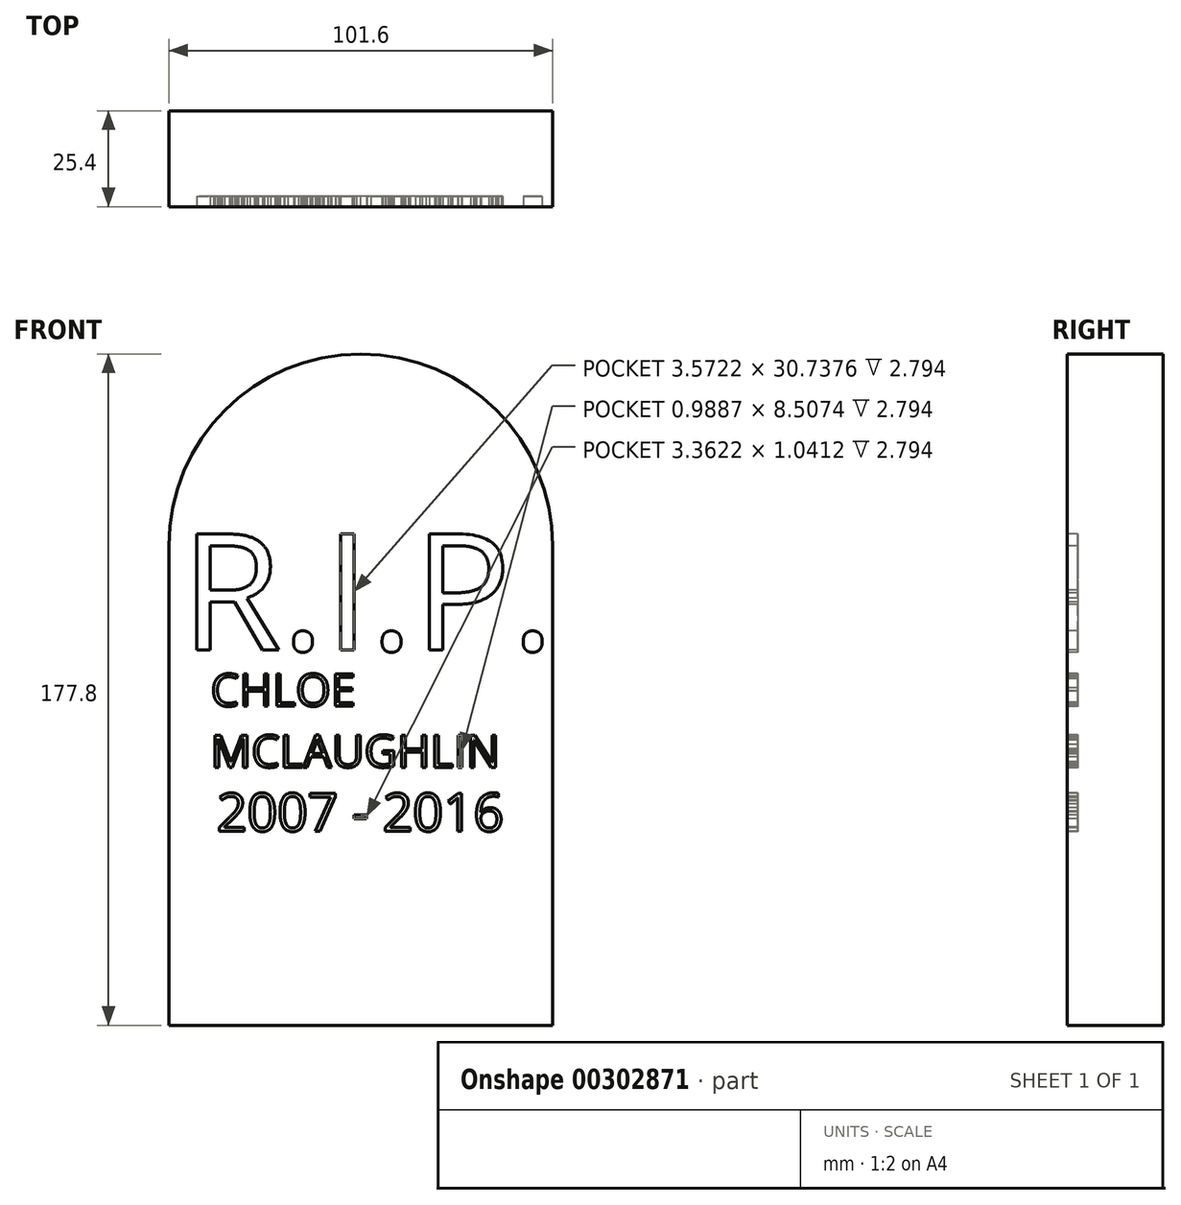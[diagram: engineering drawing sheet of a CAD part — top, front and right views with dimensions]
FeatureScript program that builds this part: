
annotation { "Feature Type Name" : "Feature", "Feature Type Description" : "" }
export const myFeature = defineFeature(function(context is Context, id is Id, definition is map)
    precondition{}
    {
        {
            var Q0;
            Q0=qCreatedBy(makeId("Front.planeOp"),FACE);
            var sketch = newSketch(context, id + "F0", { "sketchPlane" : qUnion([Q0])});
            skLineSegment(sketch, "E0", {"start": v(0, 0) * mm, "end": v(101.6, 0) * mm});
            skLineSegment(sketch, "E1", {"start": v(0, 0) * mm, "end": v(0, 127) * mm});
            skLineSegment(sketch, "E2", {"start": v(101.6, 127) * mm, "end": v(101.6, 0) * mm});
            skArc(sketch, "E3", {"start": v(101.6, 127) * mm, "mid": v(50.8, 177.8) * mm, "end": v(0, 127) * mm});
            skSolve(sketch);
        }
        {
            var Q0;
            Q0 = qSketchRegion(id + "F0", true);
            extrude(context, id + "F1", {"entities" : qUnion([Q0]), "depth" : 25.4 * mm});
        }
        {
            var Q0;
            Q0=makeQuery(id+"F1.opExtrude","CAP_FACE",FACE,{"disambiguationData":[OSD([sQuery(id+"F0.wireOp",EDGE,"E0"),sQuery(id+"F0.wireOp",EDGE,"E1"),sQuery(id+"F0.wireOp",EDGE,"E2"),sQuery(id+"F0.wireOp",EDGE,"E3")])],"isStart":false});
            var sketch = newSketch(context, id + "F2", { "sketchPlane" : qUnion([Q0])});
            skText(sketch, "E4", { "text": "R.I.P.", "fontName": "OpenSans-Regular.ttf"});
            const initialGuessF2  = {"E4": [0.00317, 0.09936, 1, 0, 0.031]};
            skSetInitialGuess(sketch, initialGuessF2);
            skSolve(sketch);
        }
        {
            var Q0;
            Q0 = qSketchRegion(id + "F2", true);
            extrude(context, id + "F3", {"entities" : qUnion([Q0]), "operationType" : NewBodyOperationType.REMOVE, "oppositeDirection" : true, "depth" : 2.8 * mm});
        }
        {
            var Q0;
            {var subQ0=sQuery(id+"F0.wireOp",EDGE,"E2");var subQ1=sQuery(id+"F0.wireOp",EDGE,"E0");var subQ2=sQuery(id+"F0.wireOp",EDGE,"E3");var subQ3=sQuery(id+"F0.wireOp",EDGE,"E1");Q0=makeQuery(id+"F3.boolean.opBoolean","SPLIT",FACE,{"disambiguationData":[TD([makeQuery(id+"F1.opExtrude","SWEPT_FACE",FACE,{"disambiguationData":[OSD([subQ1])]})])],"derivedFrom":makeQuery(id+"F1.opExtrude","CAP_FACE",FACE,{"disambiguationData":[OSD([subQ1,subQ3,subQ0,subQ2])],"isStart":false})});}
            var sketch = newSketch(context, id + "F4", { "sketchPlane" : qUnion([Q0])});
            skText(sketch, "E5", { "text": "CHLOE \nMCLAUGHLIN", "fontName": "OpenSans-Regular.ttf"});
            const initialGuessF4  = {"E5": [0.01108, 0.08453, 1, 0, 0.00858]};
            skSetInitialGuess(sketch, initialGuessF4);
            skSolve(sketch);
        }
        {
            var Q0;
            Q0 = qSketchRegion(id + "F4", true);
            var Q1;
            Q1=makeQuery(id+"F3.boolean.opBoolean","COPY",FACE,{"derivedFrom":makeQuery(id+"F3.opExtrude","CAP_FACE",FACE,{"disambiguationData":[OSD([sQuery(id+"F2.wireOp",EDGE,"E4.sketch_text.stroke-26"),sQuery(id+"F2.wireOp",EDGE,"E4.sketch_text.stroke-27"),sQuery(id+"F2.wireOp",EDGE,"E4.sketch_text.stroke-28"),sQuery(id+"F2.wireOp",EDGE,"E4.sketch_text.stroke-29")])],"isStart":false})});
            extrude(context, id + "F5", {"entities" : qUnion([Q0]), "operationType" : NewBodyOperationType.REMOVE, "endBound" : BoundingType.UP_TO_SURFACE, "oppositeDirection" : true, "endBoundEntityFace" : qUnion([Q1]), "depth" : 32.5 * mm});
        }
        {
            var Q0;
            {var subQ16=sQuery(id+"F0.wireOp",EDGE,"E0");var subQ17=makeQuery(id+"F1.opExtrude","SWEPT_FACE",FACE,{"disambiguationData":[OSD([subQ16])]});var subQ31=sQuery(id+"F0.wireOp",EDGE,"E3");var subQ34=sQuery(id+"F0.wireOp",EDGE,"E2");var subQ36=sQuery(id+"F0.wireOp",EDGE,"E1");Q0=makeQuery(id+"F5.boolean.opBoolean","SPLIT",FACE,{"disambiguationData":[TD([subQ17])],"derivedFrom":makeQuery(id+"F3.boolean.opBoolean","SPLIT",FACE,{"disambiguationData":[TD([subQ17])],"derivedFrom":makeQuery(id+"F1.opExtrude","CAP_FACE",FACE,{"disambiguationData":[OSD([subQ16,subQ36,subQ34,subQ31])],"isStart":false})})});}
            var sketch = newSketch(context, id + "F6", { "sketchPlane" : qUnion([Q0])});
            skText(sketch, "E6", { "text": "2007 - 2016", "fontName": "OpenSans-Regular.ttf"});
            const initialGuessF6  = {"E6": [0.0127, 0.0514, 1, 0, 0.0101]};
            skSetInitialGuess(sketch, initialGuessF6);
            skSolve(sketch);
        }
        {
            var Q0;
            Q0 = qSketchRegion(id + "F6", true);
            var Q1;
            Q1=makeQuery(id+"F3.boolean.opBoolean","COPY",FACE,{"derivedFrom":makeQuery(id+"F3.opExtrude","CAP_FACE",FACE,{"disambiguationData":[OSD([sQuery(id+"F2.wireOp",EDGE,"E4.sketch_text.stroke-26"),sQuery(id+"F2.wireOp",EDGE,"E4.sketch_text.stroke-27"),sQuery(id+"F2.wireOp",EDGE,"E4.sketch_text.stroke-28"),sQuery(id+"F2.wireOp",EDGE,"E4.sketch_text.stroke-29")])],"isStart":false})});
            extrude(context, id + "F7", {"entities" : qUnion([Q0]), "operationType" : NewBodyOperationType.REMOVE, "endBound" : BoundingType.UP_TO_SURFACE, "oppositeDirection" : true, "endBoundEntityFace" : qUnion([Q1]), "depth" : 25.4 * mm});
        }
    });
